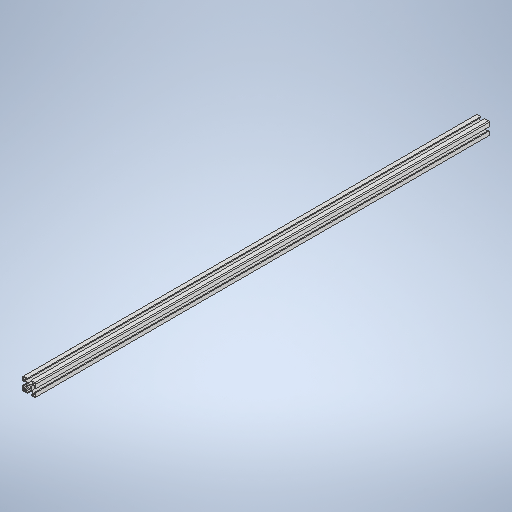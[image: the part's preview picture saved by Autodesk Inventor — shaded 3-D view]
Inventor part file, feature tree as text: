
AUTODESK INVENTOR PART (.ipt)
format: ipt  version: 2025 (Build 290162000, 162)  size: 314,880 bytes
history: native  units: in
note: dims shown in document units (in); Inventor stores cm internally (conversion verified against a paired STEP export)
features: extrude x1, sketch x1
ambient origin geometry x8: Origin, YZ Plane, XZ Plane, XY Plane, X Axis, Y Axis, Z Axis, Center Point
bodies: Solid1 (feature_tree)
feature tree (2):
  extrude  "Extrusion1"  Depth=40.9449in
  sketch  "Sketch1"  dims[d6=40.9449in d7=0.0in d8=0.1969in d9=0.0344in]
